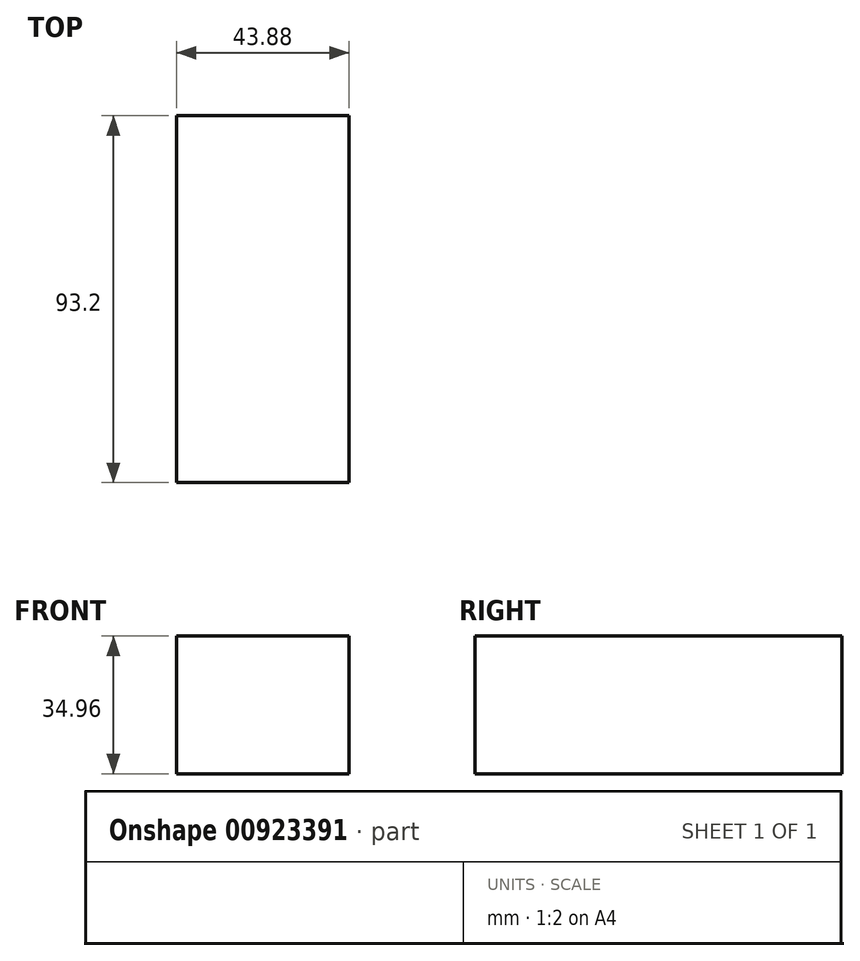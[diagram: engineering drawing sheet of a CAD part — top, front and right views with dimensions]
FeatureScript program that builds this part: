
annotation { "Feature Type Name" : "Feature", "Feature Type Description" : "" }
export const myFeature = defineFeature(function(context is Context, id is Id, definition is map)
    precondition{}
    {
        {
            var Q0;
            Q0=qCreatedBy(makeId("Front.planeOp"),FACE);
            var sketch = newSketch(context, id + "F0", { "sketchPlane" : qUnion([Q0])});
            skLineSegment(sketch, "E0.bottom", {"start": v(21.94, -17.48) * mm, "end": v(-21.94, -17.48) * mm});
            skLineSegment(sketch, "E0.top", {"start": v(21.94, 17.48) * mm, "end": v(-21.94, 17.48) * mm});
            skLineSegment(sketch, "E0.left", {"start": v(21.94, -17.48) * mm, "end": v(21.94, 17.48) * mm});
            skLineSegment(sketch, "E0.right", {"start": v(-21.94, -17.48) * mm, "end": v(-21.94, 17.48) * mm});
            skPoint(sketch, "E0.middle", {"position": v(0, 0) * mm});
            skSolve(sketch);
        }
        {
            var Q0;
            Q0=makeQuery(id+"F0.imprint","IMPRINT",FACE,{"disambiguationData":[TD([[makeQuery(id+"F0.imprint","IMPRINT",EDGE,{"derivedFrom":sQuery(id+"F0.wireOp",EDGE,"E0.bottom")}),-1.0]])]});
            extrude(context, id + "F1", {"entities" : qUnion([Q0]), "depth" : 93.2 * mm, "offsetDistance" : 25 * mm});
        }
    });
